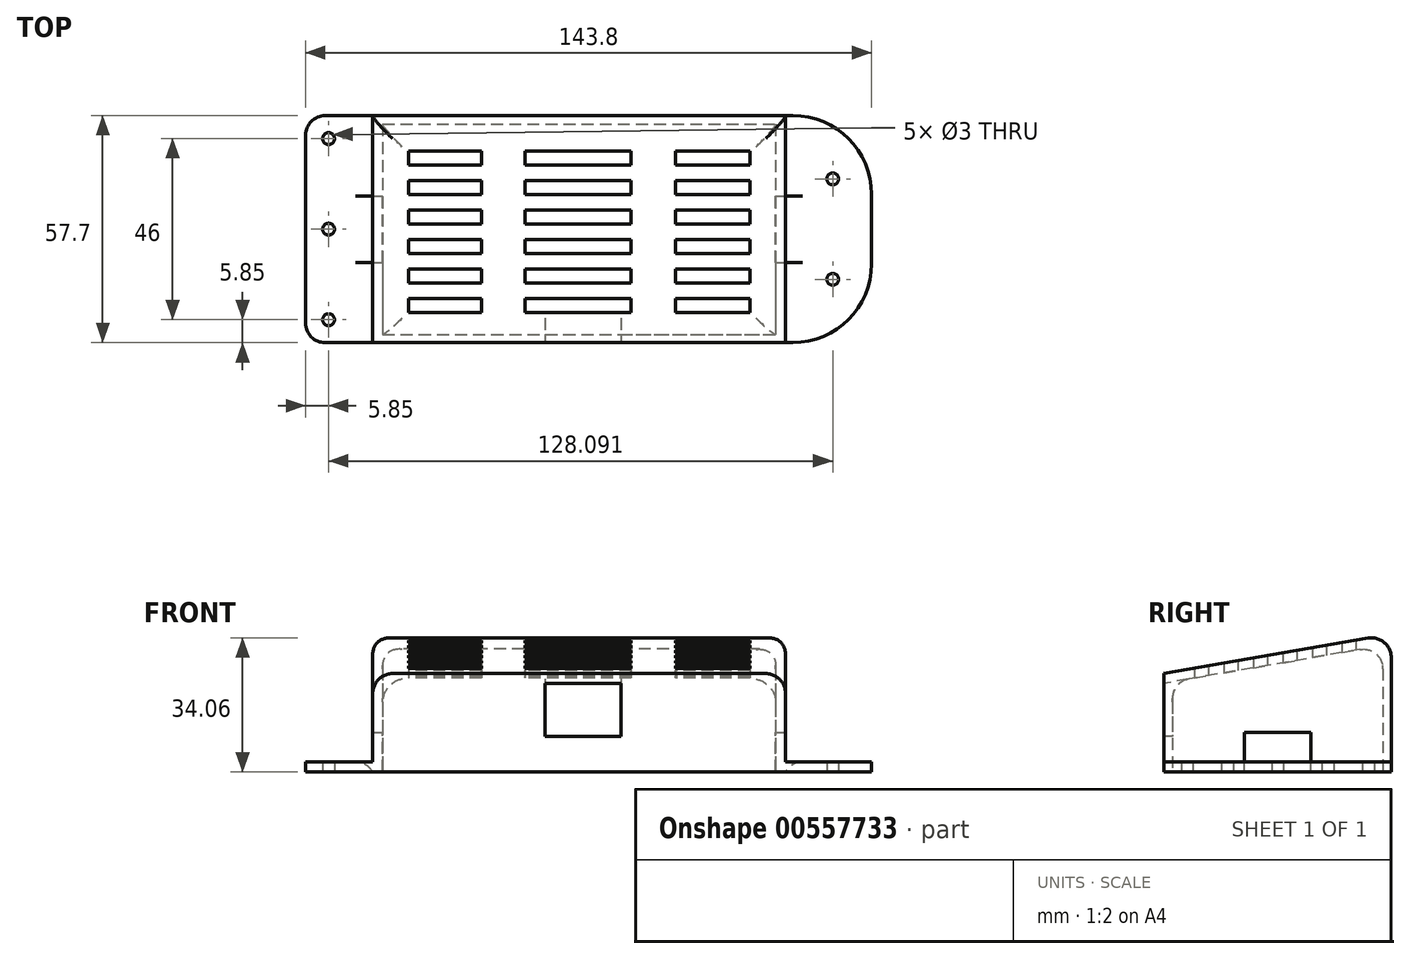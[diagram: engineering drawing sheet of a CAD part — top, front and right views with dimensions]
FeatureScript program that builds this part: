
annotation { "Feature Type Name" : "Feature", "Feature Type Description" : "" }
export const myFeature = defineFeature(function(context is Context, id is Id, definition is map)
    precondition{}
    {
        {
            var Q0;
            Q0=qCreatedBy(makeId("Top.planeOp"),FACE);
            var sketch = newSketch(context, id + "F0", { "sketchPlane" : qUnion([Q0])});
            skLineSegment(sketch, "E0.bottom", {"start": v(-51.25, 26.75) * mm, "end": v(51.25, 26.75) * mm});
            skLineSegment(sketch, "E0.top", {"start": v(-43.01, -26.75) * mm, "end": v(51.25, -26.75) * mm});
            skLineSegment(sketch, "E0.left", {"start": v(-51.25, 26.75) * mm, "end": v(-51.25, -18.51) * mm});
            skLineSegment(sketch, "E0.right", {"start": v(51.25, 26.75) * mm, "end": v(51.25, -26.75) * mm});
            skPoint(sketch, "E0.middle", {"position": v(0, 0) * mm});
            skLineSegment(sketch, "E1.0", {"start": v(-53.35, -28.85) * mm, "end": v(53.35, -28.85) * mm});
            skLineSegment(sketch, "E1.1", {"start": v(-53.35, 28.85) * mm, "end": v(-53.35, -28.85) * mm});
            skLineSegment(sketch, "E1.2", {"start": v(-53.35, 28.85) * mm, "end": v(53.35, 28.85) * mm});
            skLineSegment(sketch, "E1.3", {"start": v(53.35, 28.85) * mm, "end": v(53.35, -28.85) * mm});
            skLineSegment(sketch, "E2.bottom", {"start": v(-47.5, 23) * mm, "end": v(47.5, 23) * mm, "construction": true});
            skLineSegment(sketch, "E2.top", {"start": v(-47.5, -23) * mm, "end": v(47.5, -23) * mm, "construction": true});
            skLineSegment(sketch, "E2.left", {"start": v(-47.5, 23) * mm, "end": v(-47.5, -23) * mm, "construction": true});
            skLineSegment(sketch, "E2.right", {"start": v(47.5, 23) * mm, "end": v(47.5, -23) * mm, "construction": true});
            skCircle(sketch, "E3", {"center": v(47.5, 23) * mm, "radius": 1.5 * mm});
            skCircle(sketch, "E4", {"center": v(47.5, -23) * mm, "radius": 1.5 * mm});
            skCircle(sketch, "E5", {"center": v(-47.5, -23) * mm, "radius": 1.5 * mm});
            skCircle(sketch, "E6", {"center": v(-47.5, 23) * mm, "radius": 1.5 * mm});
            skArc(sketch, "E7", {"start": v(-51.25, 18.51) * mm, "mid": v(-43.36, 18.86) * mm, "end": v(-43.01, 26.75) * mm});
            skArc(sketch, "E8", {"start": v(43.01, 26.75) * mm, "mid": v(43.36, 18.86) * mm, "end": v(51.25, 18.51) * mm});
            skArc(sketch, "E9", {"start": v(51.25, -18.51) * mm, "mid": v(43.36, -18.86) * mm, "end": v(43.01, -26.75) * mm});
            skArc(sketch, "E10.trimOffspring", {"start": v(-43.01, -26.75) * mm, "mid": v(-43.36, -18.86) * mm, "end": v(-51.25, -18.51) * mm});
            skPoint(sketch, "E11.orphan", {"position": v(-51.25, -26.75) * mm});
            skLineSegment(sketch, "E12", {"start": v(-51.25, -18.51) * mm, "end": v(-51.25, -26.75) * mm});
            skLineSegment(sketch, "E13", {"start": v(-43.01, -26.75) * mm, "end": v(-51.25, -26.75) * mm});
            skLineSegment(sketch, "E14.bottom", {"start": v(53.35, -7.5) * mm, "end": v(-53.35, -7.5) * mm});
            skLineSegment(sketch, "E14.top", {"start": v(53.35, 7.5) * mm, "end": v(-53.35, 7.5) * mm});
            skLineSegment(sketch, "E14.left", {"start": v(53.35, -7.5) * mm, "end": v(53.35, 7.5) * mm});
            skLineSegment(sketch, "E14.right", {"start": v(-53.35, -7.5) * mm, "end": v(-53.35, 7.5) * mm});
            skLineSegment(sketch, "E15.bottom", {"start": v(-7.5, 28.85) * mm, "end": v(7.5, 28.85) * mm});
            skLineSegment(sketch, "E15.top", {"start": v(-7.5, -28.85) * mm, "end": v(7.5, -28.85) * mm});
            skLineSegment(sketch, "E15.left", {"start": v(-7.5, 28.85) * mm, "end": v(-7.5, -28.85) * mm});
            skLineSegment(sketch, "E15.right", {"start": v(7.5, 28.85) * mm, "end": v(7.5, -28.85) * mm});
            skCircle(sketch, "E16", {"center": v(-47.5, 0) * mm, "radius": 1.5 * mm});
            skCircle(sketch, "E17", {"center": v(0, 23) * mm, "radius": 1.5 * mm});
            skCircle(sketch, "E18", {"center": v(0, -23) * mm, "radius": 1.5 * mm});
            skCircle(sketch, "E19", {"center": v(47.5, 0) * mm, "radius": 1.5 * mm});
            skLineSegment(sketch, "E20", {"start": v(53.35, 28.85) * mm, "end": v(90.45, 28.85) * mm});
            skLineSegment(sketch, "E21", {"start": v(90.45, 28.85) * mm, "end": v(90.45, -28.85) * mm});
            skLineSegment(sketch, "E22", {"start": v(90.45, -28.85) * mm, "end": v(53.35, -28.85) * mm});
            skLineSegment(sketch, "E23.0", {"start": v(88.35, -26.75) * mm, "end": v(53.35, -26.75) * mm});
            skLineSegment(sketch, "E23.1", {"start": v(88.35, 26.75) * mm, "end": v(88.35, -26.75) * mm});
            skLineSegment(sketch, "E23.2", {"start": v(53.33, 26.75) * mm, "end": v(88.35, 26.75) * mm});
            skLineSegment(sketch, "E24", {"start": v(70.84, 26.75) * mm, "end": v(70.84, 0) * mm, "construction": true});
            skPoint(sketch, "E24.endSnap0", {"position": v(88.35, 0) * mm});
            skLineSegment(sketch, "E25.bottom", {"start": v(80.6, -12.75) * mm, "end": v(61.1, -12.75) * mm, "construction": true});
            skLineSegment(sketch, "E25.top", {"start": v(80.6, 12.75) * mm, "end": v(61.1, 12.75) * mm, "construction": true});
            skLineSegment(sketch, "E25.left", {"start": v(80.6, -12.75) * mm, "end": v(80.6, 12.75) * mm, "construction": true});
            skLineSegment(sketch, "E25.right", {"start": v(61.1, -12.75) * mm, "end": v(61.1, 12.75) * mm, "construction": true});
            skPoint(sketch, "E25.middle", {"position": v(70.84, 0) * mm});
            skCircle(sketch, "E26", {"center": v(61.1, 12.75) * mm, "radius": 1.5 * mm});
            skCircle(sketch, "E27", {"center": v(80.6, 12.75) * mm, "radius": 1.5 * mm});
            skCircle(sketch, "E28", {"center": v(80.6, -12.75) * mm, "radius": 1.5 * mm});
            skCircle(sketch, "E29", {"center": v(61.1, -12.75) * mm, "radius": 1.5 * mm});
            skCircle(sketch, "E30", {"center": v(61.1, 12.75) * mm, "radius": 4 * mm});
            skCircle(sketch, "E31", {"center": v(80.6, 12.75) * mm, "radius": 4 * mm});
            skCircle(sketch, "E32", {"center": v(80.6, -12.75) * mm, "radius": 4 * mm});
            skCircle(sketch, "E33", {"center": v(61.1, -12.75) * mm, "radius": 4 * mm});
            skLineSegment(sketch, "E34", {"start": v(51.25, 26.75) * mm, "end": v(51.25, 28.85) * mm});
            skLineSegment(sketch, "E35", {"start": v(51.25, -26.75) * mm, "end": v(51.25, -28.85) * mm});
            skLineSegment(sketch, "E36", {"start": v(51.25, 26.75) * mm, "end": v(53.33, 26.75) * mm});
            skLineSegment(sketch, "E37", {"start": v(51.25, -26.75) * mm, "end": v(53.35, -26.75) * mm});
            skLineSegment(sketch, "E38.bottom", {"start": v(63, 26.75) * mm, "end": v(78.7, 26.75) * mm});
            skLineSegment(sketch, "E38.top", {"start": v(63, 28.85) * mm, "end": v(78.7, 28.85) * mm});
            skLineSegment(sketch, "E38.left", {"start": v(63, 26.75) * mm, "end": v(63, 28.85) * mm});
            skLineSegment(sketch, "E38.right", {"start": v(78.7, 26.75) * mm, "end": v(78.7, 28.85) * mm});
            skPoint(sketch, "E38.middle", {"position": v(70.84, 27.8) * mm});
            skPoint(sketch, "E38.middle.positionSnap0", {"position": v(51.25, 27.8) * mm});
            skPoint(sketch, "E38.centerSnap0", {"position": v(51.25, 27.8) * mm});
            skLineSegment(sketch, "E39", {"start": v(-33.79, 28.85) * mm, "end": v(-33.79, -28.85) * mm});
            skLineSegment(sketch, "E40", {"start": v(66.08, 28.85) * mm, "end": v(66.08, -28.85) * mm});
            skLineSegment(sketch, "E41", {"start": v(-36.29, 28.85) * mm, "end": v(-36.29, -28.85) * mm});
            skLineSegment(sketch, "E42", {"start": v(68.58, 28.85) * mm, "end": v(68.58, -28.85) * mm});
            skLineSegment(sketch, "E43", {"start": v(26.76, -26.75) * mm, "end": v(26.76, -28.85) * mm});
            skSolve(sketch);
        }
        {
            var Q0;
            {var subQ0=sQuery(id+"F0.wireOp",EDGE,"E38.left");Q0=makeQuery(id+"F0.imprint","IMPRINT",FACE,{"disambiguationData":[TD([[makeQuery(id+"F0.imprint","IMPRINT",EDGE,{"derivedFrom":subQ0}),-1.0]])]});}
            var Q1;
            Q1=makeQuery(id+"F0.imprint","IMPRINT",FACE,{"disambiguationData":[TD([[makeQuery(id+"F0.imprint","IMPRINT",EDGE,{"derivedFrom":sQuery(id+"F0.wireOp",EDGE,"E18")}),-1.0]])]});
            var Q2;
            {var subQ0=sQuery(id+"F0.wireOp",EDGE,"E9");Q2=makeQuery(id+"F0.imprint","IMPRINT",FACE,{"disambiguationData":[TD([[makeQuery(id+"F0.imprint","IMPRINT",EDGE,{"derivedFrom":subQ0}),-1.0]])]});}
            var Q3;
            Q3=makeQuery(id+"F0.imprint","IMPRINT",FACE,{"disambiguationData":[TD([[makeQuery(id+"F0.imprint","IMPRINT",EDGE,{"derivedFrom":sQuery(id+"F0.wireOp",EDGE,"E19")}),-1.0]])]});
            var Q4;
            {var subQ5=sQuery(id+"F0.wireOp",EDGE,"E8");Q4=makeQuery(id+"F0.imprint","IMPRINT",FACE,{"disambiguationData":[TD([[makeQuery(id+"F0.imprint","IMPRINT",EDGE,{"derivedFrom":subQ5}),-1.0]])]});}
            var Q5;
            Q5=makeQuery(id+"F0.imprint","IMPRINT",FACE,{"disambiguationData":[TD([[makeQuery(id+"F0.imprint","IMPRINT",EDGE,{"derivedFrom":sQuery(id+"F0.wireOp",EDGE,"E17")}),-1.0]])]});
            var Q6;
            {var subQ0=sQuery(id+"F0.wireOp",EDGE,"E15.right");var subQ1=sQuery(id+"F0.wireOp",EDGE,"E14.bottom");var subQ2=makeQuery(id+"F0.imprint","INTERSECT",VERTEX,{"derivedFrom":[subQ1,subQ0]});Q6=makeQuery(id+"F0.imprint","IMPRINT",FACE,{"disambiguationData":[TD([[makeQuery(id+"F0.imprint","IMPRINT",EDGE,{"disambiguationData":[TD([[subQ2,-1.0]])],"derivedFrom":subQ1}),-1.0]])]});}
            var Q7;
            Q7=makeQuery(id+"F0.imprint","IMPRINT",FACE,{"disambiguationData":[TD([[makeQuery(id+"F0.imprint","IMPRINT",EDGE,{"derivedFrom":sQuery(id+"F0.wireOp",EDGE,"E30")}),-1.0]])]});
            var Q8;
            {var subQ7=sQuery(id+"F0.wireOp",EDGE,"E36");Q8=makeQuery(id+"F0.imprint","IMPRINT",FACE,{"disambiguationData":[TD([[makeQuery(id+"F0.imprint","IMPRINT",EDGE,{"derivedFrom":subQ7}),-1.0]])]});}
            var Q9;
            {var subQ0=sQuery(id+"F0.wireOp",EDGE,"E14.top");var subQ1=sQuery(id+"F0.wireOp",EDGE,"E0.right");var subQ2=makeQuery(id+"F0.imprint","INTERSECT",VERTEX,{"derivedFrom":[subQ1,subQ0]});Q9=makeQuery(id+"F0.imprint","IMPRINT",FACE,{"disambiguationData":[TD([[makeQuery(id+"F0.imprint","IMPRINT",EDGE,{"disambiguationData":[TD([[subQ2,-1.0]])],"derivedFrom":subQ1}),1.0]])]});}
            var Q10;
            {var subQ5=sQuery(id+"F0.wireOp",EDGE,"E37");Q10=makeQuery(id+"F0.imprint","IMPRINT",FACE,{"disambiguationData":[TD([[makeQuery(id+"F0.imprint","IMPRINT",EDGE,{"derivedFrom":subQ5}),1.0]])]});}
            var Q11;
            Q11=makeQuery(id+"F0.imprint","IMPRINT",FACE,{"disambiguationData":[TD([[makeQuery(id+"F0.imprint","IMPRINT",EDGE,{"derivedFrom":sQuery(id+"F0.wireOp",EDGE,"E4")}),-1.0]])]});
            var Q12;
            Q12=makeQuery(id+"F0.imprint","IMPRINT",FACE,{"disambiguationData":[TD([[makeQuery(id+"F0.imprint","IMPRINT",EDGE,{"derivedFrom":sQuery(id+"F0.wireOp",EDGE,"E29")}),-1.0]])]});
            var Q13;
            Q13=makeQuery(id+"F0.imprint","IMPRINT",FACE,{"disambiguationData":[TD([[makeQuery(id+"F0.imprint","IMPRINT",EDGE,{"derivedFrom":sQuery(id+"F0.wireOp",EDGE,"E3")}),-1.0]])]});
            var Q14;
            Q14=makeQuery(id+"F0.imprint","IMPRINT",FACE,{"disambiguationData":[TD([[makeQuery(id+"F0.imprint","IMPRINT",EDGE,{"derivedFrom":sQuery(id+"F0.wireOp",EDGE,"E26")}),-1.0]])]});
            var Q15;
            Q15=makeQuery(id+"F0.imprint","IMPRINT",FACE,{"disambiguationData":[TD([[makeQuery(id+"F0.imprint","IMPRINT",EDGE,{"derivedFrom":sQuery(id+"F0.wireOp",EDGE,"E17")}),1.0]])]});
            var Q16;
            Q16=makeQuery(id+"F0.imprint","IMPRINT",FACE,{"disambiguationData":[TD([[makeQuery(id+"F0.imprint","IMPRINT",EDGE,{"derivedFrom":sQuery(id+"F0.wireOp",EDGE,"E18")}),1.0]])]});
            var Q17;
            Q17=makeQuery(id+"F0.imprint","IMPRINT",FACE,{"disambiguationData":[TD([[makeQuery(id+"F0.imprint","IMPRINT",EDGE,{"derivedFrom":sQuery(id+"F0.wireOp",EDGE,"E4")}),1.0]])]});
            var Q18;
            Q18=makeQuery(id+"F0.imprint","IMPRINT",FACE,{"disambiguationData":[TD([[makeQuery(id+"F0.imprint","IMPRINT",EDGE,{"derivedFrom":sQuery(id+"F0.wireOp",EDGE,"E19")}),1.0]])]});
            var Q19;
            Q19=makeQuery(id+"F0.imprint","IMPRINT",FACE,{"disambiguationData":[TD([[makeQuery(id+"F0.imprint","IMPRINT",EDGE,{"derivedFrom":sQuery(id+"F0.wireOp",EDGE,"E3")}),1.0]])]});
            var Q20;
            Q20=makeQuery(id+"F0.imprint","IMPRINT",FACE,{"disambiguationData":[TD([[makeQuery(id+"F0.imprint","IMPRINT",EDGE,{"derivedFrom":sQuery(id+"F0.wireOp",EDGE,"E26")}),1.0]])]});
            var Q21;
            Q21=makeQuery(id+"F0.imprint","IMPRINT",FACE,{"disambiguationData":[TD([[makeQuery(id+"F0.imprint","IMPRINT",EDGE,{"derivedFrom":sQuery(id+"F0.wireOp",EDGE,"E29")}),1.0]])]});
            var Q22;
            {var subQ5=sQuery(id+"F0.wireOp",EDGE,"E34");Q22=makeQuery(id+"F0.imprint","IMPRINT",FACE,{"disambiguationData":[TD([[makeQuery(id+"F0.imprint","IMPRINT",EDGE,{"derivedFrom":subQ5}),1.0]])]});}
            var Q23;
            {var subQ0=sQuery(id+"F0.wireOp",EDGE,"E34");Q23=makeQuery(id+"F0.imprint","IMPRINT",FACE,{"disambiguationData":[TD([[makeQuery(id+"F0.imprint","IMPRINT",EDGE,{"derivedFrom":subQ0}),-1.0]])]});}
            var Q24;
            {var subQ5=sQuery(id+"F0.wireOp",EDGE,"E38.left");Q24=makeQuery(id+"F0.imprint","IMPRINT",FACE,{"disambiguationData":[TD([[makeQuery(id+"F0.imprint","IMPRINT",EDGE,{"derivedFrom":subQ5}),1.0]])]});}
            var Q25;
            {var subQ3=sQuery(id+"F0.wireOp",EDGE,"E35");Q25=makeQuery(id+"F0.imprint","IMPRINT",FACE,{"disambiguationData":[TD([[makeQuery(id+"F0.imprint","IMPRINT",EDGE,{"derivedFrom":subQ3}),1.0]])]});}
            var Q26;
            {var subQ0=sQuery(id+"F0.wireOp",EDGE,"E35");Q26=makeQuery(id+"F0.imprint","IMPRINT",FACE,{"disambiguationData":[TD([[makeQuery(id+"F0.imprint","IMPRINT",EDGE,{"derivedFrom":subQ0}),-1.0]])]});}
            var Q27;
            {var subQ0=sQuery(id+"F0.wireOp",EDGE,"E15.left");var subQ1=sQuery(id+"F0.wireOp",EDGE,"E0.top");var subQ2=makeQuery(id+"F0.imprint","INTERSECT",VERTEX,{"derivedFrom":[subQ1,subQ0]});Q27=makeQuery(id+"F0.imprint","IMPRINT",FACE,{"disambiguationData":[TD([[makeQuery(id+"F0.imprint","IMPRINT",EDGE,{"disambiguationData":[TD([[subQ2,-1.0]])],"derivedFrom":subQ1}),-1.0]])]});}
            var Q28;
            {var subQ0=sQuery(id+"F0.wireOp",EDGE,"E39");var subQ1=sQuery(id+"F0.wireOp",EDGE,"E0.top");var subQ2=makeQuery(id+"F0.imprint","INTERSECT",VERTEX,{"derivedFrom":[subQ1,subQ0]});Q28=makeQuery(id+"F0.imprint","IMPRINT",FACE,{"disambiguationData":[TD([[makeQuery(id+"F0.imprint","IMPRINT",EDGE,{"disambiguationData":[TD([[subQ2,-1.0]])],"derivedFrom":subQ1}),1.0]])]});}
            var Q29;
            {var subQ0=sQuery(id+"F0.wireOp",EDGE,"E39");var subQ1=sQuery(id+"F0.wireOp",EDGE,"E0.top");var subQ2=makeQuery(id+"F0.imprint","INTERSECT",VERTEX,{"derivedFrom":[subQ1,subQ0]});Q29=makeQuery(id+"F0.imprint","IMPRINT",FACE,{"disambiguationData":[TD([[makeQuery(id+"F0.imprint","IMPRINT",EDGE,{"disambiguationData":[TD([[subQ2,-1.0]])],"derivedFrom":subQ1}),-1.0]])]});}
            var Q30;
            {var subQ0=sQuery(id+"F0.wireOp",EDGE,"E39");var subQ1=sQuery(id+"F0.wireOp",EDGE,"E0.bottom");var subQ2=makeQuery(id+"F0.imprint","INTERSECT",VERTEX,{"derivedFrom":[subQ1,subQ0]});Q30=makeQuery(id+"F0.imprint","IMPRINT",FACE,{"disambiguationData":[TD([[makeQuery(id+"F0.imprint","IMPRINT",EDGE,{"disambiguationData":[TD([[subQ2,-1.0]])],"derivedFrom":subQ1}),-1.0]])]});}
            var Q31;
            {var subQ0=sQuery(id+"F0.wireOp",EDGE,"E39");var subQ1=sQuery(id+"F0.wireOp",EDGE,"E0.bottom");var subQ2=makeQuery(id+"F0.imprint","INTERSECT",VERTEX,{"derivedFrom":[subQ1,subQ0]});Q31=makeQuery(id+"F0.imprint","IMPRINT",FACE,{"disambiguationData":[TD([[makeQuery(id+"F0.imprint","IMPRINT",EDGE,{"disambiguationData":[TD([[subQ2,-1.0]])],"derivedFrom":subQ1}),1.0]])]});}
            var Q32;
            {var subQ0=sQuery(id+"F0.wireOp",EDGE,"E39");var subQ1=sQuery(id+"F0.wireOp",EDGE,"E14.bottom");var subQ2=makeQuery(id+"F0.imprint","INTERSECT",VERTEX,{"derivedFrom":[subQ1,subQ0]});Q32=makeQuery(id+"F0.imprint","IMPRINT",FACE,{"disambiguationData":[TD([[makeQuery(id+"F0.imprint","IMPRINT",EDGE,{"disambiguationData":[TD([[subQ2,1.0]])],"derivedFrom":subQ1}),-1.0]])]});}
            var Q33;
            {var subQ0=sQuery(id+"F0.wireOp",EDGE,"E22");var subQ5=sQuery(id+"F0.wireOp",EDGE,"E40");var subQ6=makeQuery(id+"F0.imprint","INTERSECT",VERTEX,{"derivedFrom":[subQ0,subQ5]});Q33=makeQuery(id+"F0.imprint","IMPRINT",FACE,{"disambiguationData":[TD([[makeQuery(id+"F0.imprint","IMPRINT",EDGE,{"disambiguationData":[TD([[subQ6,1.0]])],"derivedFrom":subQ5}),-1.0]])]});}
            var Q34;
            {var subQ0=sQuery(id+"F0.wireOp",EDGE,"E40");var subQ1=sQuery(id+"F0.wireOp",EDGE,"E22");var subQ2=makeQuery(id+"F0.imprint","INTERSECT",VERTEX,{"derivedFrom":[subQ1,subQ0]});Q34=makeQuery(id+"F0.imprint","IMPRINT",FACE,{"disambiguationData":[TD([[makeQuery(id+"F0.imprint","IMPRINT",EDGE,{"disambiguationData":[TD([[subQ2,1.0]])],"derivedFrom":subQ1}),-1.0]])]});}
            var Q35;
            {var subQ0=sQuery(id+"F0.wireOp",EDGE,"E40");var subQ1=sQuery(id+"F0.wireOp",EDGE,"E23.0");var subQ2=makeQuery(id+"F0.imprint","INTERSECT",VERTEX,{"derivedFrom":[subQ1,subQ0]});Q35=makeQuery(id+"F0.imprint","IMPRINT",FACE,{"disambiguationData":[TD([[makeQuery(id+"F0.imprint","IMPRINT",EDGE,{"disambiguationData":[TD([[subQ2,1.0]])],"derivedFrom":subQ1}),-1.0]])]});}
            var Q36;
            {var subQ0=sQuery(id+"F0.wireOp",EDGE,"E42");var subQ1=sQuery(id+"F0.wireOp",EDGE,"E20");var subQ2=makeQuery(id+"F0.imprint","INTERSECT",VERTEX,{"derivedFrom":[subQ1,subQ0]});Q36=makeQuery(id+"F0.imprint","IMPRINT",FACE,{"disambiguationData":[TD([[makeQuery(id+"F0.imprint","IMPRINT",EDGE,{"disambiguationData":[TD([[subQ2,1.0]])],"derivedFrom":subQ1}),-1.0]])]});}
            var Q37;
            {var subQ0=sQuery(id+"F0.wireOp",EDGE,"E39");var subQ1=sQuery(id+"F0.wireOp",EDGE,"E0.bottom");var subQ2=makeQuery(id+"F0.imprint","INTERSECT",VERTEX,{"derivedFrom":[subQ1,subQ0]});Q37=makeQuery(id+"F0.imprint","IMPRINT",FACE,{"disambiguationData":[TD([[makeQuery(id+"F0.imprint","IMPRINT",EDGE,{"disambiguationData":[TD([[subQ2,1.0]])],"derivedFrom":subQ1}),1.0]])]});}
            var Q38;
            {var subQ0=sQuery(id+"F0.wireOp",EDGE,"E39");var subQ1=sQuery(id+"F0.wireOp",EDGE,"E0.bottom");var subQ2=makeQuery(id+"F0.imprint","INTERSECT",VERTEX,{"derivedFrom":[subQ1,subQ0]});Q38=makeQuery(id+"F0.imprint","IMPRINT",FACE,{"disambiguationData":[TD([[makeQuery(id+"F0.imprint","IMPRINT",EDGE,{"disambiguationData":[TD([[subQ2,1.0]])],"derivedFrom":subQ1}),-1.0]])]});}
            var Q39;
            {var subQ0=sQuery(id+"F0.wireOp",EDGE,"E39");var subQ1=sQuery(id+"F0.wireOp",EDGE,"E0.top");var subQ2=makeQuery(id+"F0.imprint","INTERSECT",VERTEX,{"derivedFrom":[subQ1,subQ0]});Q39=makeQuery(id+"F0.imprint","IMPRINT",FACE,{"disambiguationData":[TD([[makeQuery(id+"F0.imprint","IMPRINT",EDGE,{"disambiguationData":[TD([[subQ2,1.0]])],"derivedFrom":subQ1}),-1.0]])]});}
            var Q40;
            {var subQ0=sQuery(id+"F0.wireOp",EDGE,"E39");var subQ1=sQuery(id+"F0.wireOp",EDGE,"E0.top");var subQ2=makeQuery(id+"F0.imprint","INTERSECT",VERTEX,{"derivedFrom":[subQ1,subQ0]});Q40=makeQuery(id+"F0.imprint","IMPRINT",FACE,{"disambiguationData":[TD([[makeQuery(id+"F0.imprint","IMPRINT",EDGE,{"disambiguationData":[TD([[subQ2,1.0]])],"derivedFrom":subQ1}),1.0]])]});}
            var Q41;
            {var subQ0=sQuery(id+"F0.wireOp",EDGE,"E39");var subQ1=sQuery(id+"F0.wireOp",EDGE,"E14.bottom");var subQ2=makeQuery(id+"F0.imprint","INTERSECT",VERTEX,{"derivedFrom":[subQ1,subQ0]});Q41=makeQuery(id+"F0.imprint","IMPRINT",FACE,{"disambiguationData":[TD([[makeQuery(id+"F0.imprint","IMPRINT",EDGE,{"disambiguationData":[TD([[subQ2,-1.0]])],"derivedFrom":subQ1}),-1.0]])]});}
            var Q42;
            {var subQ0=sQuery(id+"F0.wireOp",EDGE,"E15.right");var subQ1=sQuery(id+"F0.wireOp",EDGE,"E0.bottom");var subQ2=makeQuery(id+"F0.imprint","INTERSECT",VERTEX,{"derivedFrom":[subQ1,subQ0]});Q42=makeQuery(id+"F0.imprint","IMPRINT",FACE,{"disambiguationData":[TD([[makeQuery(id+"F0.imprint","IMPRINT",EDGE,{"disambiguationData":[TD([[subQ2,1.0]])],"derivedFrom":subQ1}),1.0]])]});}
            var Q43;
            {var subQ0=sQuery(id+"F0.wireOp",EDGE,"E43");Q43=makeQuery(id+"F0.imprint","IMPRINT",FACE,{"disambiguationData":[TD([[makeQuery(id+"F0.imprint","IMPRINT",EDGE,{"derivedFrom":subQ0}),-1.0]])]});}
            extrude(context, id + "F1", {"entities" : qUnion([Q0, Q1, Q2, Q3, Q4, Q5, Q6, Q7, Q8, Q9, Q10, Q11, Q12, Q13, Q14, Q15, Q16, Q17, Q18, Q19, Q20, Q21, Q22, Q23, Q24, Q25, Q26, Q27, Q28, Q29, Q30, Q31, Q32, Q33, Q34, Q35, Q36, Q37, Q38, Q39, Q40, Q41, Q42, Q43]), "depth" : 35 * mm, "offsetDistance" : 25 * mm});
        }
        {
            var Q0;
            Q0=qCreatedBy(makeId("Right.planeOp"),FACE);
            var sketch = newSketch(context, id + "F2", { "sketchPlane" : qUnion([Q0])});
            skLineSegment(sketch, "E44", {"start": v(0, 0) * mm, "end": v(-28.85, 0) * mm, "construction": true});
            skLineSegment(sketch, "E45", {"start": v(-28.85, 0) * mm, "end": v(-28.85, 25) * mm, "construction": true});
            skLineSegment(sketch, "E46", {"start": v(0, 0) * mm, "end": v(0, 10) * mm, "construction": true});
            skLineSegment(sketch, "E47.MirrorCS", {"start": v(0, 0) * mm, "end": v(28.85, 0) * mm, "construction": true});
            skLineSegment(sketch, "E48", {"start": v(28.85, 0) * mm, "end": v(28.85, 35) * mm});
            skLineSegment(sketch, "E49", {"start": v(28.85, 35) * mm, "end": v(-28.85, 25) * mm});
            skLineSegment(sketch, "E50", {"start": v(-28.85, 35) * mm, "end": v(28.85, 35) * mm});
            skLineSegment(sketch, "E51", {"start": v(-28.85, 35) * mm, "end": v(-28.85, 25) * mm});
            skLineSegment(sketch, "E52.bottom", {"start": v(8.46, 10) * mm, "end": v(-8.46, 10) * mm});
            skLineSegment(sketch, "E52.top", {"start": v(8.46, -10) * mm, "end": v(-8.46, -10) * mm});
            skLineSegment(sketch, "E52.left", {"start": v(8.46, 10) * mm, "end": v(8.46, -10) * mm});
            skLineSegment(sketch, "E52.right", {"start": v(-8.46, 10) * mm, "end": v(-8.46, -10) * mm});
            skPoint(sketch, "E52.middle", {"position": v(0, 0) * mm});
            skSolve(sketch);
        }
        {
            var Q0;
            Q0=makeQuery(id+"F2.imprint","IMPRINT",FACE,{"disambiguationData":[TD([[makeQuery(id+"F2.imprint","IMPRINT",EDGE,{"derivedFrom":sQuery(id+"F2.wireOp",EDGE,"E49")}),-1.0]])]});
            var Q1;
            Q1=makeQuery(id+"F2.imprint","IMPRINT",FACE,{"disambiguationData":[TD([[makeQuery(id+"F2.imprint","IMPRINT",EDGE,{"derivedFrom":sQuery(id+"F2.wireOp",EDGE,"E52.bottom")}),1.0]])]});
            extrude(context, id + "F3", {"entities" : qUnion([Q0, Q1]), "operationType" : NewBodyOperationType.REMOVE, "endBound" : BoundingType.THROUGH_ALL, "oppositeDirection" : true, "depth" : 25 * mm, "offsetDistance" : 25 * mm, "hasSecondDirection" : true, "secondDirectionBound" : SecondDirectionBoundingType.THROUGH_ALL, "secondDirectionOppositeDirection" : false, "secondDirectionDepth" : 25 * mm});
        }
        {
            var Q0;
            Q0=makeQuery(id+"F0.imprint","IMPRINT",FACE,{"disambiguationData":[TD([[makeQuery(id+"F0.imprint","IMPRINT",EDGE,{"derivedFrom":sQuery(id+"F0.wireOp",EDGE,"E18")}),-1.0]])]});
            var Q1;
            {var subQ0=sQuery(id+"F0.wireOp",EDGE,"E9");Q1=makeQuery(id+"F0.imprint","IMPRINT",FACE,{"disambiguationData":[TD([[makeQuery(id+"F0.imprint","IMPRINT",EDGE,{"derivedFrom":subQ0}),-1.0]])]});}
            var Q2;
            Q2=makeQuery(id+"F0.imprint","IMPRINT",FACE,{"disambiguationData":[TD([[makeQuery(id+"F0.imprint","IMPRINT",EDGE,{"derivedFrom":sQuery(id+"F0.wireOp",EDGE,"E19")}),-1.0]])]});
            var Q3;
            {var subQ0=sQuery(id+"F0.wireOp",EDGE,"E15.right");var subQ1=sQuery(id+"F0.wireOp",EDGE,"E14.bottom");var subQ2=makeQuery(id+"F0.imprint","INTERSECT",VERTEX,{"derivedFrom":[subQ1,subQ0]});Q3=makeQuery(id+"F0.imprint","IMPRINT",FACE,{"disambiguationData":[TD([[makeQuery(id+"F0.imprint","IMPRINT",EDGE,{"disambiguationData":[TD([[subQ2,-1.0]])],"derivedFrom":subQ1}),-1.0]])]});}
            var Q4;
            Q4=makeQuery(id+"F0.imprint","IMPRINT",FACE,{"disambiguationData":[TD([[makeQuery(id+"F0.imprint","IMPRINT",EDGE,{"derivedFrom":sQuery(id+"F0.wireOp",EDGE,"E17")}),-1.0]])]});
            var Q5;
            {var subQ5=sQuery(id+"F0.wireOp",EDGE,"E8");Q5=makeQuery(id+"F0.imprint","IMPRINT",FACE,{"disambiguationData":[TD([[makeQuery(id+"F0.imprint","IMPRINT",EDGE,{"derivedFrom":subQ5}),-1.0]])]});}
            var Q6;
            Q6=makeQuery(id+"F0.imprint","IMPRINT",FACE,{"disambiguationData":[TD([[makeQuery(id+"F0.imprint","IMPRINT",EDGE,{"derivedFrom":sQuery(id+"F0.wireOp",EDGE,"E18")}),1.0]])]});
            var Q7;
            Q7=makeQuery(id+"F0.imprint","IMPRINT",FACE,{"disambiguationData":[TD([[makeQuery(id+"F0.imprint","IMPRINT",EDGE,{"derivedFrom":sQuery(id+"F0.wireOp",EDGE,"E17")}),1.0]])]});
            var Q8;
            Q8=makeQuery(id+"F0.imprint","IMPRINT",FACE,{"disambiguationData":[TD([[makeQuery(id+"F0.imprint","IMPRINT",EDGE,{"derivedFrom":sQuery(id+"F0.wireOp",EDGE,"E3")}),1.0]])]});
            var Q9;
            Q9=makeQuery(id+"F0.imprint","IMPRINT",FACE,{"disambiguationData":[TD([[makeQuery(id+"F0.imprint","IMPRINT",EDGE,{"derivedFrom":sQuery(id+"F0.wireOp",EDGE,"E4")}),-1.0]])]});
            var Q10;
            Q10=makeQuery(id+"F0.imprint","IMPRINT",FACE,{"disambiguationData":[TD([[makeQuery(id+"F0.imprint","IMPRINT",EDGE,{"derivedFrom":sQuery(id+"F0.wireOp",EDGE,"E4")}),1.0]])]});
            var Q11;
            Q11=makeQuery(id+"F0.imprint","IMPRINT",FACE,{"disambiguationData":[TD([[makeQuery(id+"F0.imprint","IMPRINT",EDGE,{"derivedFrom":sQuery(id+"F0.wireOp",EDGE,"E19")}),1.0]])]});
            var Q12;
            {var subQ7=sQuery(id+"F0.wireOp",EDGE,"E36");Q12=makeQuery(id+"F0.imprint","IMPRINT",FACE,{"disambiguationData":[TD([[makeQuery(id+"F0.imprint","IMPRINT",EDGE,{"derivedFrom":subQ7}),-1.0]])]});}
            var Q13;
            {var subQ0=sQuery(id+"F0.wireOp",EDGE,"E14.top");var subQ1=sQuery(id+"F0.wireOp",EDGE,"E0.right");var subQ2=makeQuery(id+"F0.imprint","INTERSECT",VERTEX,{"derivedFrom":[subQ1,subQ0]});Q13=makeQuery(id+"F0.imprint","IMPRINT",FACE,{"disambiguationData":[TD([[makeQuery(id+"F0.imprint","IMPRINT",EDGE,{"disambiguationData":[TD([[subQ2,-1.0]])],"derivedFrom":subQ1}),1.0]])]});}
            var Q14;
            {var subQ5=sQuery(id+"F0.wireOp",EDGE,"E37");Q14=makeQuery(id+"F0.imprint","IMPRINT",FACE,{"disambiguationData":[TD([[makeQuery(id+"F0.imprint","IMPRINT",EDGE,{"derivedFrom":subQ5}),1.0]])]});}
            var Q15;
            Q15=makeQuery(id+"F0.imprint","IMPRINT",FACE,{"disambiguationData":[TD([[makeQuery(id+"F0.imprint","IMPRINT",EDGE,{"derivedFrom":sQuery(id+"F0.wireOp",EDGE,"E3")}),-1.0]])]});
            var Q16;
            {var subQ0=sQuery(id+"F0.wireOp",EDGE,"E39");var subQ1=sQuery(id+"F0.wireOp",EDGE,"E0.top");var subQ2=makeQuery(id+"F0.imprint","INTERSECT",VERTEX,{"derivedFrom":[subQ1,subQ0]});Q16=makeQuery(id+"F0.imprint","IMPRINT",FACE,{"disambiguationData":[TD([[makeQuery(id+"F0.imprint","IMPRINT",EDGE,{"disambiguationData":[TD([[subQ2,-1.0]])],"derivedFrom":subQ1}),1.0]])]});}
            var Q17;
            {var subQ0=sQuery(id+"F0.wireOp",EDGE,"E39");var subQ1=sQuery(id+"F0.wireOp",EDGE,"E14.bottom");var subQ2=makeQuery(id+"F0.imprint","INTERSECT",VERTEX,{"derivedFrom":[subQ1,subQ0]});Q17=makeQuery(id+"F0.imprint","IMPRINT",FACE,{"disambiguationData":[TD([[makeQuery(id+"F0.imprint","IMPRINT",EDGE,{"disambiguationData":[TD([[subQ2,1.0]])],"derivedFrom":subQ1}),-1.0]])]});}
            var Q18;
            {var subQ0=sQuery(id+"F0.wireOp",EDGE,"E39");var subQ1=sQuery(id+"F0.wireOp",EDGE,"E0.bottom");var subQ2=makeQuery(id+"F0.imprint","INTERSECT",VERTEX,{"derivedFrom":[subQ1,subQ0]});Q18=makeQuery(id+"F0.imprint","IMPRINT",FACE,{"disambiguationData":[TD([[makeQuery(id+"F0.imprint","IMPRINT",EDGE,{"disambiguationData":[TD([[subQ2,-1.0]])],"derivedFrom":subQ1}),-1.0]])]});}
            var Q19;
            Q19=makeQuery(id+"F0.imprint","IMPRINT",FACE,{"disambiguationData":[TD([[makeQuery(id+"F0.imprint","IMPRINT",EDGE,{"derivedFrom":sQuery(id+"F0.wireOp",EDGE,"E30")}),-1.0]])]});
            var Q20;
            Q20=makeQuery(id+"F0.imprint","IMPRINT",FACE,{"disambiguationData":[TD([[makeQuery(id+"F0.imprint","IMPRINT",EDGE,{"derivedFrom":sQuery(id+"F0.wireOp",EDGE,"E26")}),1.0]])]});
            var Q21;
            Q21=makeQuery(id+"F0.imprint","IMPRINT",FACE,{"disambiguationData":[TD([[makeQuery(id+"F0.imprint","IMPRINT",EDGE,{"derivedFrom":sQuery(id+"F0.wireOp",EDGE,"E29")}),1.0]])]});
            var Q22;
            Q22=makeQuery(id+"F0.imprint","IMPRINT",FACE,{"disambiguationData":[TD([[makeQuery(id+"F0.imprint","IMPRINT",EDGE,{"derivedFrom":sQuery(id+"F0.wireOp",EDGE,"E29")}),-1.0]])]});
            var Q23;
            Q23=makeQuery(id+"F0.imprint","IMPRINT",FACE,{"disambiguationData":[TD([[makeQuery(id+"F0.imprint","IMPRINT",EDGE,{"derivedFrom":sQuery(id+"F0.wireOp",EDGE,"E26")}),-1.0]])]});
            var Q24;
            {var subQ0=sQuery(id+"F0.wireOp",EDGE,"E43");Q24=makeQuery(id+"F0.imprint","IMPRINT",FACE,{"disambiguationData":[TD([[makeQuery(id+"F0.imprint","IMPRINT",EDGE,{"derivedFrom":subQ0}),-1.0]])]});}
            var Q25;
            Q25=makeQuery(id+"F3.boolean.opBoolean","COPY",FACE,{"derivedFrom":makeQuery(id+"F3.opExtrude","SWEPT_FACE",FACE,{"disambiguationData":[OSD([sQuery(id+"F2.wireOp",EDGE,"E49")])]})});
            extrude(context, id + "F4", {"entities" : qUnion([Q0, Q1, Q2, Q3, Q4, Q5, Q6, Q7, Q8, Q9, Q10, Q11, Q12, Q13, Q14, Q15, Q16, Q17, Q18, Q19, Q20, Q21, Q22, Q23, Q24]), "operationType" : NewBodyOperationType.REMOVE, "endBound" : BoundingType.UP_TO_SURFACE, "depth" : (35 - 2.5) * mm, "endBoundEntityFace" : qUnion([Q25]), "hasOffset" : true, "offsetDistance" : 2.5 * mm});
        }
        {
            var Q0;
            {var subQ5=sQuery(id+"F0.wireOp",EDGE,"E12");Q0=makeQuery(id+"F0.imprint","IMPRINT",FACE,{"disambiguationData":[TD([[makeQuery(id+"F0.imprint","IMPRINT",EDGE,{"derivedFrom":subQ5}),-1.0]])]});}
            var Q1;
            Q1=makeQuery(id+"F0.imprint","IMPRINT",FACE,{"disambiguationData":[TD([[makeQuery(id+"F0.imprint","IMPRINT",EDGE,{"derivedFrom":sQuery(id+"F0.wireOp",EDGE,"E5")}),-1.0]])]});
            var Q2;
            {var subQ0=sQuery(id+"F0.wireOp",EDGE,"E10.trimOffspring");Q2=makeQuery(id+"F0.imprint","IMPRINT",FACE,{"disambiguationData":[TD([[makeQuery(id+"F0.imprint","IMPRINT",EDGE,{"derivedFrom":subQ0}),-1.0]])]});}
            var Q3;
            Q3=makeQuery(id+"F0.imprint","IMPRINT",FACE,{"disambiguationData":[TD([[makeQuery(id+"F0.imprint","IMPRINT",EDGE,{"derivedFrom":sQuery(id+"F0.wireOp",EDGE,"E16")}),-1.0]])]});
            var Q4;
            {var subQ5=sQuery(id+"F0.wireOp",EDGE,"E7");Q4=makeQuery(id+"F0.imprint","IMPRINT",FACE,{"disambiguationData":[TD([[makeQuery(id+"F0.imprint","IMPRINT",EDGE,{"derivedFrom":subQ5}),-1.0]])]});}
            var Q5;
            {var subQ0=sQuery(id+"F0.wireOp",EDGE,"E7");var subQ3=sQuery(id+"F0.wireOp",EDGE,"E0.bottom");var subQ11=makeQuery(id+"F0.imprint","INTERSECT",VERTEX,{"derivedFrom":[subQ3,subQ0]});Q5=makeQuery(id+"F0.imprint","IMPRINT",FACE,{"disambiguationData":[TD([[makeQuery(id+"F0.imprint","IMPRINT",EDGE,{"disambiguationData":[TD([[subQ11,1.0]])],"derivedFrom":subQ3}),1.0]])]});}
            var Q6;
            Q6=makeQuery(id+"F0.imprint","IMPRINT",FACE,{"disambiguationData":[TD([[makeQuery(id+"F0.imprint","IMPRINT",EDGE,{"derivedFrom":sQuery(id+"F0.wireOp",EDGE,"E6")}),-1.0]])]});
            var Q7;
            {var subQ0=sQuery(id+"F0.wireOp",EDGE,"E14.top");var subQ1=sQuery(id+"F0.wireOp",EDGE,"E0.left");var subQ2=makeQuery(id+"F0.imprint","INTERSECT",VERTEX,{"derivedFrom":[subQ1,subQ0]});Q7=makeQuery(id+"F0.imprint","IMPRINT",FACE,{"disambiguationData":[TD([[makeQuery(id+"F0.imprint","IMPRINT",EDGE,{"disambiguationData":[TD([[subQ2,-1.0]])],"derivedFrom":subQ1}),-1.0]])]});}
            var Q8;
            {var subQ6=sQuery(id+"F0.wireOp",EDGE,"E23.1");Q8=makeQuery(id+"F0.imprint","IMPRINT",FACE,{"disambiguationData":[TD([[makeQuery(id+"F0.imprint","IMPRINT",EDGE,{"derivedFrom":subQ6}),-1.0]])]});}
            var Q9;
            {var subQ5=sQuery(id+"F0.wireOp",EDGE,"E21");Q9=makeQuery(id+"F0.imprint","IMPRINT",FACE,{"disambiguationData":[TD([[makeQuery(id+"F0.imprint","IMPRINT",EDGE,{"derivedFrom":subQ5}),-1.0]])]});}
            var Q10;
            Q10=makeQuery(id+"F0.imprint","IMPRINT",FACE,{"disambiguationData":[TD([[makeQuery(id+"F0.imprint","IMPRINT",EDGE,{"derivedFrom":sQuery(id+"F0.wireOp",EDGE,"E27")}),-1.0]])]});
            var Q11;
            Q11=makeQuery(id+"F0.imprint","IMPRINT",FACE,{"disambiguationData":[TD([[makeQuery(id+"F0.imprint","IMPRINT",EDGE,{"derivedFrom":sQuery(id+"F0.wireOp",EDGE,"E28")}),-1.0]])]});
            var Q12;
            {var subQ0=sQuery(id+"F0.wireOp",EDGE,"E38.right");Q12=makeQuery(id+"F0.imprint","IMPRINT",FACE,{"disambiguationData":[TD([[makeQuery(id+"F0.imprint","IMPRINT",EDGE,{"derivedFrom":subQ0}),1.0]])]});}
            extrude(context, id + "F5", {"entities" : qUnion([Q0, Q1, Q2, Q3, Q4, Q5, Q6, Q7, Q8, Q9, Q10, Q11, Q12]), "operationType" : NewBodyOperationType.ADD, "depth" : 2.5 * mm, "offsetDistance" : 25 * mm});
        }
        {
            var Q0;
            Q0=makeQuery(id+"F5.opExtrude","SWEPT_EDGE",EDGE,{"disambiguationData":[OSD([sQuery(id+"F0.wireOp",EDGE,"E21"),sQuery(id+"F0.wireOp",EDGE,"E22")])]});
            var Q1;
            Q1=makeQuery(id+"F5.opExtrude","SWEPT_EDGE",EDGE,{"disambiguationData":[OSD([sQuery(id+"F0.wireOp",EDGE,"E20"),sQuery(id+"F0.wireOp",EDGE,"E21")])]});
            fillet(context, id + "F6", {"entities" : qUnion([Q0, Q1]), "radius" : 20 * mm, "tangentPropagation" : true, "allowEdgeOverflow" : false});
        }
        {
            var Q0;
            Q0=makeQuery(id+"F5.opExtrude","SWEPT_EDGE",EDGE,{"disambiguationData":[OSD([sQuery(id+"F0.wireOp",EDGE,"E1.1"),sQuery(id+"F0.wireOp",EDGE,"E1.2")])]});
            var Q1;
            Q1=makeQuery(id+"F5.opExtrude","SWEPT_EDGE",EDGE,{"disambiguationData":[OSD([sQuery(id+"F0.wireOp",EDGE,"E1.0"),sQuery(id+"F0.wireOp",EDGE,"E1.1")])]});
            var Q2;
            Q2=makeQuery(id+"F3.boolean.opBoolean","COPY",EDGE,{"derivedFrom":makeQuery(id+"F3.opExtrude","SWEPT_EDGE",EDGE,{"disambiguationData":[OSD([sQuery(id+"F2.wireOp",EDGE,"E49"),sQuery(id+"F2.wireOp",EDGE,"E51")])]})});
            var Q3;
            Q3=makeQuery(id+"F3.boolean.opBoolean","MERGE",EDGE,{"derivedFrom":[makeQuery(id+"F1.opExtrude","CAP_EDGE",EDGE,{"disambiguationData":[OSD([sQuery(id+"F0.wireOp",EDGE,"E1.2"),sQuery(id+"F0.wireOp",EDGE,"E20")])],"isStart":false})],"fromTools":[makeQuery(id+"F3.opExtrude","SWEPT_EDGE",EDGE,{"disambiguationData":[OSD([sQuery(id+"F2.wireOp",EDGE,"E49"),sQuery(id+"F2.wireOp",EDGE,"E50")])]})]});
            var Q4;
            {var subQ0=sQuery(id+"F0.wireOp",EDGE,"E0.top");Q4=qUnion([makeQuery(id+"F4.boolean.opBoolean","COPY",EDGE,{"derivedFrom":makeQuery(id+"F4.opExtrude","CAP_EDGE",EDGE,{"disambiguationData":[OSD([subQ0])],"isStart":false})}),makeQuery(id+"F4.boolean.opBoolean","COPY",EDGE,{"derivedFrom":makeQuery(id+"F4.opExtrude","CAP_EDGE",EDGE,{"disambiguationData":[OSD([subQ0,sQuery(id+"F0.wireOp",EDGE,"E23.0"),sQuery(id+"F0.wireOp",EDGE,"E37")])],"isStart":false})})]);}
            var Q5;
            Q5=makeQuery(id+"F4.boolean.opBoolean","COPY",EDGE,{"derivedFrom":makeQuery(id+"F4.opExtrude","CAP_EDGE",EDGE,{"disambiguationData":[OSD([sQuery(id+"F0.wireOp",EDGE,"E0.bottom"),sQuery(id+"F0.wireOp",EDGE,"E23.2"),sQuery(id+"F0.wireOp",EDGE,"E36")])],"isStart":false})});
            var Q6;
            Q6=makeQuery(id+"F3.boolean.opBoolean","INTERSECT",EDGE,{"derivedFrom":[makeQuery(id+"F1.opExtrude","SWEPT_FACE",FACE,{"disambiguationData":[OSD([sQuery(id+"F0.wireOp",EDGE,"E42")])]}),makeQuery(id+"F3.opExtrude","SWEPT_FACE",FACE,{"disambiguationData":[OSD([sQuery(id+"F2.wireOp",EDGE,"E49")])]})]});
            var Q7;
            Q7=makeQuery(id+"F4.boolean.opBoolean","COPY",EDGE,{"derivedFrom":makeQuery(id+"F4.opExtrude","CAP_EDGE",EDGE,{"disambiguationData":[OSD([sQuery(id+"F0.wireOp",EDGE,"E40")])],"isStart":false})});
            var Q8;
            Q8=makeQuery(id+"F4.boolean.opBoolean","COPY",EDGE,{"derivedFrom":makeQuery(id+"F4.opExtrude","CAP_EDGE",EDGE,{"disambiguationData":[OSD([sQuery(id+"F0.wireOp",EDGE,"E39")])],"isStart":false})});
            var Q9;
            Q9=makeQuery(id+"F3.boolean.opBoolean","INTERSECT",EDGE,{"derivedFrom":[makeQuery(id+"F1.opExtrude","SWEPT_FACE",FACE,{"disambiguationData":[OSD([sQuery(id+"F0.wireOp",EDGE,"E41")])]}),makeQuery(id+"F3.opExtrude","SWEPT_FACE",FACE,{"disambiguationData":[OSD([sQuery(id+"F2.wireOp",EDGE,"E49")])]})]});
            var Q10;
            {var subQ0=sQuery(id+"F0.wireOp",EDGE,"E42");var subQ1=makeQuery(id+"F1.opExtrude","SWEPT_FACE",FACE,{"disambiguationData":[OSD([subQ0])]});var subQ2=sQuery(id+"F0.wireOp",EDGE,"E22");var subQ3=makeQuery(id+"F5.opExtrude","CAP_FACE",FACE,{"disambiguationData":[OSD([sQuery(id+"F0.wireOp",EDGE,"E20"),sQuery(id+"F0.wireOp",EDGE,"E21"),subQ2,sQuery(id+"F0.wireOp",EDGE,"E27"),sQuery(id+"F0.wireOp",EDGE,"E28"),subQ0])],"isStart":false});Q10=makeQuery(id+"F5.boolean.opBoolean","SPLIT",EDGE,{"disambiguationData":[topologyDisambiguationEdgeConnected([subQ1,subQ3]),TD([makeQuery(id+"F3.boolean.opBoolean","COPY",FACE,{"derivedFrom":makeQuery(id+"F3.opExtrude","SWEPT_FACE",FACE,{"disambiguationData":[OSD([sQuery(id+"F2.wireOp",EDGE,"E52.right")])]})})])],"derivedFrom":makeQuery(id+"F5.opExtrude","CAP_EDGE",EDGE,{"disambiguationData":[OSD([subQ0])],"isStart":false})});}
            var Q11;
            {var subQ1=sQuery(id+"F0.wireOp",EDGE,"E42");var subQ2=makeQuery(id+"F1.opExtrude","SWEPT_FACE",FACE,{"disambiguationData":[OSD([subQ1])]});var subQ3=sQuery(id+"F0.wireOp",EDGE,"E20");var subQ4=makeQuery(id+"F5.opExtrude","CAP_FACE",FACE,{"disambiguationData":[OSD([subQ3,sQuery(id+"F0.wireOp",EDGE,"E21"),sQuery(id+"F0.wireOp",EDGE,"E22"),sQuery(id+"F0.wireOp",EDGE,"E27"),sQuery(id+"F0.wireOp",EDGE,"E28"),subQ1])],"isStart":false});Q11=makeQuery(id+"F5.boolean.opBoolean","SPLIT",EDGE,{"disambiguationData":[topologyDisambiguationEdgeConnected([subQ2,subQ4]),TD([makeQuery(id+"F3.boolean.opBoolean","COPY",FACE,{"derivedFrom":makeQuery(id+"F3.opExtrude","SWEPT_FACE",FACE,{"disambiguationData":[OSD([sQuery(id+"F2.wireOp",EDGE,"E52.left")])]})})])],"derivedFrom":makeQuery(id+"F5.opExtrude","CAP_EDGE",EDGE,{"disambiguationData":[OSD([subQ1])],"isStart":false})});}
            var Q12;
            {var subQ0=sQuery(id+"F0.wireOp",EDGE,"E41");var subQ1=makeQuery(id+"F1.opExtrude","SWEPT_FACE",FACE,{"disambiguationData":[OSD([subQ0])]});var subQ2=sQuery(id+"F0.wireOp",EDGE,"E1.0");var subQ3=makeQuery(id+"F5.opExtrude","CAP_FACE",FACE,{"disambiguationData":[OSD([subQ2,sQuery(id+"F0.wireOp",EDGE,"E1.1"),sQuery(id+"F0.wireOp",EDGE,"E1.2"),sQuery(id+"F0.wireOp",EDGE,"E5"),sQuery(id+"F0.wireOp",EDGE,"E6"),sQuery(id+"F0.wireOp",EDGE,"E16"),subQ0])],"isStart":false});Q12=makeQuery(id+"F5.boolean.opBoolean","SPLIT",EDGE,{"disambiguationData":[topologyDisambiguationEdgeConnected([subQ1,subQ3]),TD([makeQuery(id+"F3.boolean.opBoolean","COPY",FACE,{"derivedFrom":makeQuery(id+"F3.opExtrude","SWEPT_FACE",FACE,{"disambiguationData":[OSD([sQuery(id+"F2.wireOp",EDGE,"E52.right")])]})})])],"derivedFrom":makeQuery(id+"F5.opExtrude","CAP_EDGE",EDGE,{"disambiguationData":[OSD([subQ0])],"isStart":false})});}
            var Q13;
            {var subQ0=sQuery(id+"F0.wireOp",EDGE,"E41");var subQ1=sQuery(id+"F0.wireOp",EDGE,"E1.2");var subQ2=makeQuery(id+"F5.opExtrude","CAP_FACE",FACE,{"disambiguationData":[OSD([sQuery(id+"F0.wireOp",EDGE,"E1.0"),sQuery(id+"F0.wireOp",EDGE,"E1.1"),subQ1,sQuery(id+"F0.wireOp",EDGE,"E5"),sQuery(id+"F0.wireOp",EDGE,"E6"),sQuery(id+"F0.wireOp",EDGE,"E16"),subQ0])],"isStart":false});var subQ3=makeQuery(id+"F1.opExtrude","SWEPT_FACE",FACE,{"disambiguationData":[OSD([subQ0])]});Q13=makeQuery(id+"F5.boolean.opBoolean","SPLIT",EDGE,{"disambiguationData":[topologyDisambiguationEdgeConnected([subQ3,subQ2]),TD([makeQuery(id+"F3.boolean.opBoolean","COPY",FACE,{"derivedFrom":makeQuery(id+"F3.opExtrude","SWEPT_FACE",FACE,{"disambiguationData":[OSD([sQuery(id+"F2.wireOp",EDGE,"E52.left")])]})})])],"derivedFrom":makeQuery(id+"F5.opExtrude","CAP_EDGE",EDGE,{"disambiguationData":[OSD([subQ0])],"isStart":false})});}
            fillet(context, id + "F7", {"entities" : qUnion([Q0, Q1, Q2, Q3, Q4, Q5, Q6, Q7, Q8, Q9, Q10, Q11, Q12, Q13]), "radius" : 5 * mm, "tangentPropagation" : true, "allowEdgeOverflow" : false});
        }
        {
            var Q0;
            {var subQ0=sQuery(id+"F0.wireOp",EDGE,"E43");Q0=makeQuery(id+"F0.imprint","IMPRINT",FACE,{"disambiguationData":[TD([[makeQuery(id+"F0.imprint","IMPRINT",EDGE,{"derivedFrom":subQ0}),-1.0]])]});}
            extrude(context, id + "F8", {"entities" : qUnion([Q0]), "operationType" : NewBodyOperationType.ADD, "depth" : 9 * mm, "offsetDistance" : 25 * mm});
        }
        {
            var Q0;
            Q0=qCreatedBy(makeId("Top.planeOp"),FACE);
            var sketch = newSketch(context, id + "F9", { "sketchPlane" : qUnion([Q0])});
            skLineSegment(sketch, "E53.bottom", {"start": v(-27.2, -21.16) * mm, "end": v(59.5, -21.16) * mm});
            skLineSegment(sketch, "E53.top", {"start": v(-27.2, -17.6) * mm, "end": v(59.5, -17.6) * mm});
            skLineSegment(sketch, "E53.left", {"start": v(-27.2, -21.16) * mm, "end": v(-27.2, -17.6) * mm});
            skLineSegment(sketch, "E53.right", {"start": v(59.5, -21.16) * mm, "end": v(59.5, -17.6) * mm});
            skLineSegment(sketch, "E54.0.1.0", {"start": v(-27.2, -13.66) * mm, "end": v(-27.2, -10.1) * mm});
            skLineSegment(sketch, "E54.0.1.1", {"start": v(-27.2, -10.1) * mm, "end": v(59.5, -10.1) * mm});
            skLineSegment(sketch, "E54.0.1.2", {"start": v(-27.2, -13.66) * mm, "end": v(59.5, -13.66) * mm});
            skLineSegment(sketch, "E54.0.1.3", {"start": v(59.5, -13.66) * mm, "end": v(59.5, -10.1) * mm});
            skLineSegment(sketch, "E54.0.2.0", {"start": v(-27.2, -6.16) * mm, "end": v(-27.2, -2.6) * mm});
            skLineSegment(sketch, "E54.0.2.1", {"start": v(-27.2, -2.6) * mm, "end": v(59.5, -2.6) * mm});
            skLineSegment(sketch, "E54.0.2.2", {"start": v(-27.2, -6.16) * mm, "end": v(59.5, -6.16) * mm});
            skLineSegment(sketch, "E54.0.2.3", {"start": v(59.5, -6.16) * mm, "end": v(59.5, -2.6) * mm});
            skLineSegment(sketch, "E54.0.3.0", {"start": v(-27.2, 1.34) * mm, "end": v(-27.2, 4.9) * mm});
            skLineSegment(sketch, "E54.0.3.1", {"start": v(-27.2, 4.9) * mm, "end": v(59.5, 4.9) * mm});
            skLineSegment(sketch, "E54.0.3.2", {"start": v(-27.2, 1.34) * mm, "end": v(59.5, 1.34) * mm});
            skLineSegment(sketch, "E54.0.3.3", {"start": v(59.5, 1.34) * mm, "end": v(59.5, 4.9) * mm});
            skLineSegment(sketch, "E54.0.4.0", {"start": v(-27.2, 8.84) * mm, "end": v(-27.2, 12.4) * mm});
            skLineSegment(sketch, "E54.0.4.1", {"start": v(-27.2, 12.4) * mm, "end": v(59.5, 12.4) * mm});
            skLineSegment(sketch, "E54.0.4.2", {"start": v(-27.2, 8.84) * mm, "end": v(59.5, 8.84) * mm});
            skLineSegment(sketch, "E54.0.4.3", {"start": v(59.5, 8.84) * mm, "end": v(59.5, 12.4) * mm});
            skLineSegment(sketch, "E54.0.5.0", {"start": v(-27.2, 16.34) * mm, "end": v(-27.2, 19.9) * mm});
            skLineSegment(sketch, "E54.0.5.1", {"start": v(-27.2, 19.9) * mm, "end": v(59.5, 19.9) * mm});
            skLineSegment(sketch, "E54.0.5.2", {"start": v(-27.2, 16.34) * mm, "end": v(59.5, 16.34) * mm});
            skLineSegment(sketch, "E54.0.5.3", {"start": v(59.5, 16.34) * mm, "end": v(59.5, 19.9) * mm});
            skLineSegment(sketch, "E54.direction1", {"start": v(-27.2, -21.16) * mm, "end": v(-2.2, -21.16) * mm, "construction": true});
            skLineSegment(sketch, "E54.direction2", {"start": v(-27.2, -21.16) * mm, "end": v(-27.2, -13.66) * mm, "construction": true});
            skLineSegment(sketch, "E55.bottom", {"start": v(-8.66, 19.9) * mm, "end": v(2.39, 19.9) * mm});
            skLineSegment(sketch, "E55.top", {"start": v(-8.66, -21.16) * mm, "end": v(2.39, -21.16) * mm});
            skLineSegment(sketch, "E55.left", {"start": v(-8.66, 19.9) * mm, "end": v(-8.66, -21.16) * mm});
            skLineSegment(sketch, "E55.right", {"start": v(2.39, 19.9) * mm, "end": v(2.39, -21.16) * mm});
            skLineSegment(sketch, "E56.bottom", {"start": v(29.36, 19.9) * mm, "end": v(40.6, 19.9) * mm});
            skLineSegment(sketch, "E56.top", {"start": v(29.36, -21.16) * mm, "end": v(40.6, -21.16) * mm});
            skLineSegment(sketch, "E56.left", {"start": v(29.36, 19.9) * mm, "end": v(29.36, -21.16) * mm});
            skLineSegment(sketch, "E56.right", {"start": v(40.6, 19.9) * mm, "end": v(40.6, -21.16) * mm});
            skSolve(sketch);
        }
        {
            var Q0;
            {var subQ0=sQuery(id+"F9.wireOp",EDGE,"E54.0.5.0");Q0=makeQuery(id+"F9.imprint","IMPRINT",FACE,{"disambiguationData":[TD([[makeQuery(id+"F9.imprint","IMPRINT",EDGE,{"derivedFrom":subQ0}),-1.0]])]});}
            var Q1;
            {var subQ0=sQuery(id+"F9.wireOp",EDGE,"E55.right");var subQ1=sQuery(id+"F9.wireOp",EDGE,"E54.0.5.1");var subQ2=makeQuery(id+"F9.imprint","INTERSECT",VERTEX,{"derivedFrom":[subQ1,subQ0]});Q1=makeQuery(id+"F9.imprint","IMPRINT",FACE,{"disambiguationData":[TD([[makeQuery(id+"F9.imprint","IMPRINT",EDGE,{"disambiguationData":[TD([[subQ2,-1.0]])],"derivedFrom":subQ1}),-1.0]])]});}
            var Q2;
            {var subQ0=sQuery(id+"F9.wireOp",EDGE,"E54.0.5.3");Q2=makeQuery(id+"F9.imprint","IMPRINT",FACE,{"disambiguationData":[TD([[makeQuery(id+"F9.imprint","IMPRINT",EDGE,{"derivedFrom":subQ0}),1.0]])]});}
            var Q3;
            {var subQ0=sQuery(id+"F9.wireOp",EDGE,"E54.0.4.0");Q3=makeQuery(id+"F9.imprint","IMPRINT",FACE,{"disambiguationData":[TD([[makeQuery(id+"F9.imprint","IMPRINT",EDGE,{"derivedFrom":subQ0}),-1.0]])]});}
            var Q4;
            {var subQ0=sQuery(id+"F9.wireOp",EDGE,"E54.0.3.0");Q4=makeQuery(id+"F9.imprint","IMPRINT",FACE,{"disambiguationData":[TD([[makeQuery(id+"F9.imprint","IMPRINT",EDGE,{"derivedFrom":subQ0}),-1.0]])]});}
            var Q5;
            {var subQ0=sQuery(id+"F9.wireOp",EDGE,"E54.0.2.0");Q5=makeQuery(id+"F9.imprint","IMPRINT",FACE,{"disambiguationData":[TD([[makeQuery(id+"F9.imprint","IMPRINT",EDGE,{"derivedFrom":subQ0}),-1.0]])]});}
            var Q6;
            {var subQ0=sQuery(id+"F9.wireOp",EDGE,"E54.0.1.0");Q6=makeQuery(id+"F9.imprint","IMPRINT",FACE,{"disambiguationData":[TD([[makeQuery(id+"F9.imprint","IMPRINT",EDGE,{"derivedFrom":subQ0}),-1.0]])]});}
            var Q7;
            {var subQ0=sQuery(id+"F9.wireOp",EDGE,"E53.left");Q7=makeQuery(id+"F9.imprint","IMPRINT",FACE,{"disambiguationData":[TD([[makeQuery(id+"F9.imprint","IMPRINT",EDGE,{"derivedFrom":subQ0}),-1.0]])]});}
            var Q8;
            {var subQ0=sQuery(id+"F9.wireOp",EDGE,"E53.right");Q8=makeQuery(id+"F9.imprint","IMPRINT",FACE,{"disambiguationData":[TD([[makeQuery(id+"F9.imprint","IMPRINT",EDGE,{"derivedFrom":subQ0}),1.0]])]});}
            var Q9;
            {var subQ0=sQuery(id+"F9.wireOp",EDGE,"E54.0.1.3");Q9=makeQuery(id+"F9.imprint","IMPRINT",FACE,{"disambiguationData":[TD([[makeQuery(id+"F9.imprint","IMPRINT",EDGE,{"derivedFrom":subQ0}),1.0]])]});}
            var Q10;
            {var subQ0=sQuery(id+"F9.wireOp",EDGE,"E54.0.2.3");Q10=makeQuery(id+"F9.imprint","IMPRINT",FACE,{"disambiguationData":[TD([[makeQuery(id+"F9.imprint","IMPRINT",EDGE,{"derivedFrom":subQ0}),1.0]])]});}
            var Q11;
            {var subQ0=sQuery(id+"F9.wireOp",EDGE,"E54.0.3.3");Q11=makeQuery(id+"F9.imprint","IMPRINT",FACE,{"disambiguationData":[TD([[makeQuery(id+"F9.imprint","IMPRINT",EDGE,{"derivedFrom":subQ0}),1.0]])]});}
            var Q12;
            {var subQ0=sQuery(id+"F9.wireOp",EDGE,"E54.0.4.3");Q12=makeQuery(id+"F9.imprint","IMPRINT",FACE,{"disambiguationData":[TD([[makeQuery(id+"F9.imprint","IMPRINT",EDGE,{"derivedFrom":subQ0}),1.0]])]});}
            var Q13;
            {var subQ0=sQuery(id+"F9.wireOp",EDGE,"E55.right");var subQ1=sQuery(id+"F9.wireOp",EDGE,"E54.0.4.1");var subQ2=makeQuery(id+"F9.imprint","INTERSECT",VERTEX,{"derivedFrom":[subQ1,subQ0]});Q13=makeQuery(id+"F9.imprint","IMPRINT",FACE,{"disambiguationData":[TD([[makeQuery(id+"F9.imprint","IMPRINT",EDGE,{"disambiguationData":[TD([[subQ2,-1.0]])],"derivedFrom":subQ1}),-1.0]])]});}
            var Q14;
            {var subQ0=sQuery(id+"F9.wireOp",EDGE,"E55.right");var subQ1=sQuery(id+"F9.wireOp",EDGE,"E54.0.3.1");var subQ2=makeQuery(id+"F9.imprint","INTERSECT",VERTEX,{"derivedFrom":[subQ1,subQ0]});Q14=makeQuery(id+"F9.imprint","IMPRINT",FACE,{"disambiguationData":[TD([[makeQuery(id+"F9.imprint","IMPRINT",EDGE,{"disambiguationData":[TD([[subQ2,-1.0]])],"derivedFrom":subQ1}),-1.0]])]});}
            var Q15;
            {var subQ0=sQuery(id+"F9.wireOp",EDGE,"E55.right");var subQ1=sQuery(id+"F9.wireOp",EDGE,"E54.0.2.1");var subQ2=makeQuery(id+"F9.imprint","INTERSECT",VERTEX,{"derivedFrom":[subQ1,subQ0]});Q15=makeQuery(id+"F9.imprint","IMPRINT",FACE,{"disambiguationData":[TD([[makeQuery(id+"F9.imprint","IMPRINT",EDGE,{"disambiguationData":[TD([[subQ2,-1.0]])],"derivedFrom":subQ1}),-1.0]])]});}
            var Q16;
            {var subQ0=sQuery(id+"F9.wireOp",EDGE,"E55.right");var subQ1=sQuery(id+"F9.wireOp",EDGE,"E54.0.1.1");var subQ2=makeQuery(id+"F9.imprint","INTERSECT",VERTEX,{"derivedFrom":[subQ1,subQ0]});Q16=makeQuery(id+"F9.imprint","IMPRINT",FACE,{"disambiguationData":[TD([[makeQuery(id+"F9.imprint","IMPRINT",EDGE,{"disambiguationData":[TD([[subQ2,-1.0]])],"derivedFrom":subQ1}),-1.0]])]});}
            var Q17;
            {var subQ0=sQuery(id+"F9.wireOp",EDGE,"E55.right");var subQ1=sQuery(id+"F9.wireOp",EDGE,"E53.bottom");var subQ2=makeQuery(id+"F9.imprint","INTERSECT",VERTEX,{"derivedFrom":[subQ1,subQ0]});Q17=makeQuery(id+"F9.imprint","IMPRINT",FACE,{"disambiguationData":[TD([[makeQuery(id+"F9.imprint","IMPRINT",EDGE,{"disambiguationData":[TD([[subQ2,-1.0]])],"derivedFrom":subQ1}),1.0]])]});}
            extrude(context, id + "F10", {"entities" : qUnion([Q0, Q1, Q2, Q3, Q4, Q5, Q6, Q7, Q8, Q9, Q10, Q11, Q12, Q13, Q14, Q15, Q16, Q17]), "operationType" : NewBodyOperationType.REMOVE, "endBound" : BoundingType.THROUGH_ALL, "depth" : 25 * mm, "offsetDistance" : 25 * mm});
        }
    });
